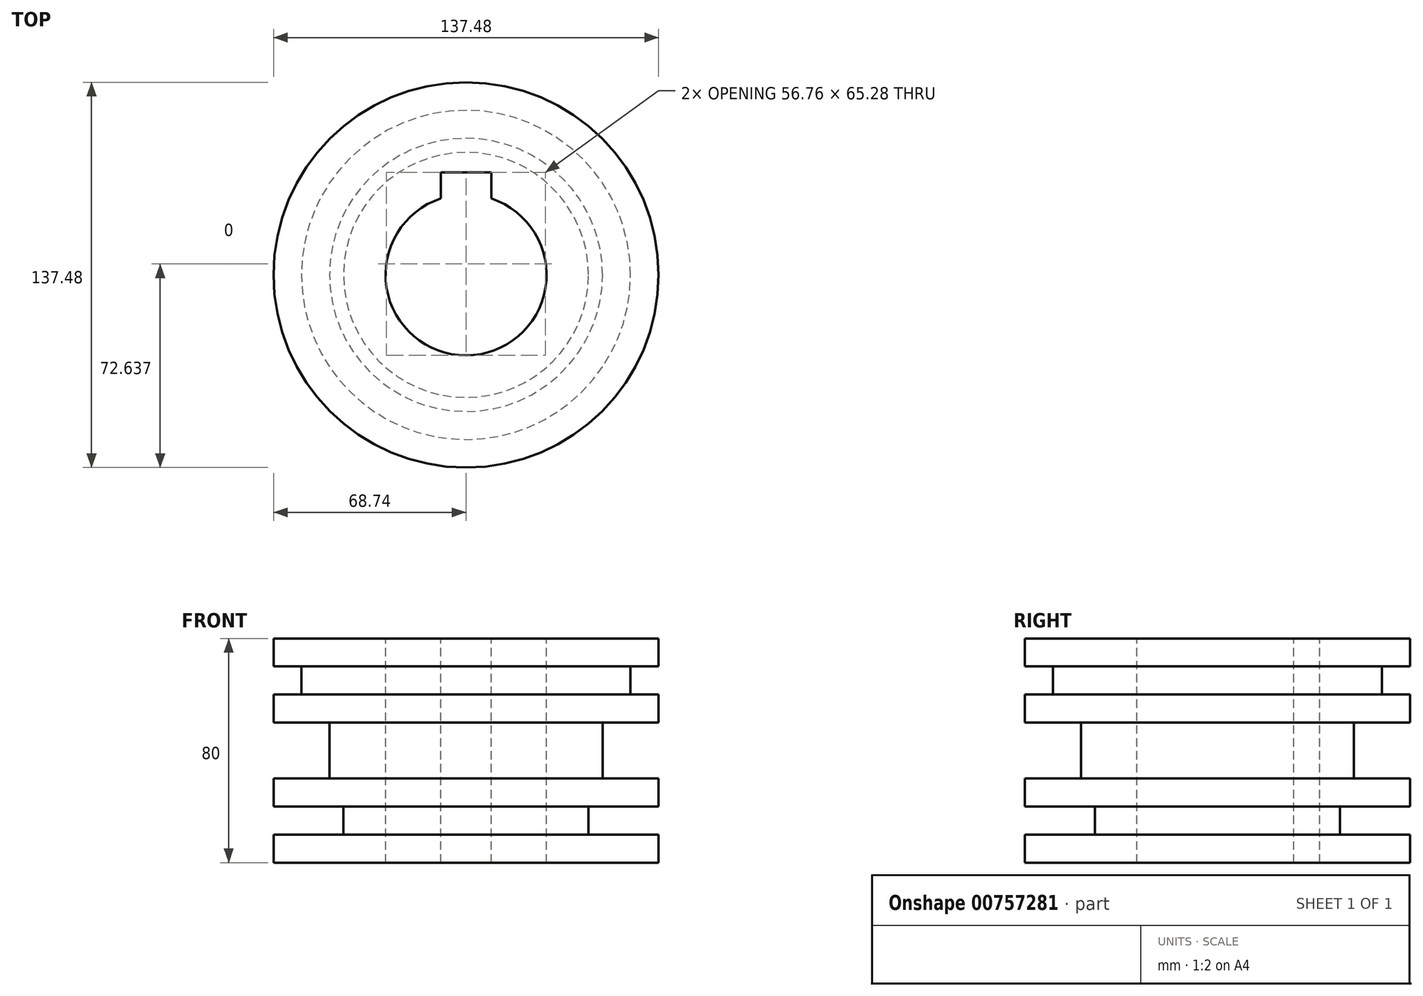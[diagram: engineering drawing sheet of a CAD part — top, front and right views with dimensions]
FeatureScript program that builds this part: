
annotation { "Feature Type Name" : "Feature", "Feature Type Description" : "" }
export const myFeature = defineFeature(function(context is Context, id is Id, definition is map)
    precondition{}
    {
        {
            var Q0;
            Q0=qCreatedBy(makeId("Front.planeOp"),FACE);
            var sketch = newSketch(context, id + "F0", { "sketchPlane" : qUnion([Q0])});
            skLineSegment(sketch, "E0", {"start": v(28.74, 0) * mm, "end": v(28.74, -80) * mm});
            skLineSegment(sketch, "E1", {"start": v(28.74, 0) * mm, "end": v(68.74, 0) * mm});
            skLineSegment(sketch, "E2", {"start": v(68.74, 0) * mm, "end": v(68.74, -10) * mm});
            skLineSegment(sketch, "E3", {"start": v(68.74, -10) * mm, "end": v(58.74, -10) * mm});
            skLineSegment(sketch, "E4", {"start": v(58.74, -10) * mm, "end": v(58.74, -20) * mm});
            skLineSegment(sketch, "E5", {"start": v(58.74, -20) * mm, "end": v(68.74, -20) * mm});
            skLineSegment(sketch, "E6", {"start": v(68.74, -20) * mm, "end": v(68.74, -30) * mm});
            skLineSegment(sketch, "E7", {"start": v(68.74, -30) * mm, "end": v(48.74, -30) * mm});
            skLineSegment(sketch, "E8", {"start": v(48.74, -30) * mm, "end": v(48.74, -50) * mm});
            skLineSegment(sketch, "E9", {"start": v(48.74, -50) * mm, "end": v(68.74, -50) * mm});
            skLineSegment(sketch, "E10", {"start": v(68.74, -50) * mm, "end": v(68.74, -60) * mm});
            skLineSegment(sketch, "E11", {"start": v(68.74, -60) * mm, "end": v(43.74, -60) * mm});
            skLineSegment(sketch, "E12", {"start": v(43.74, -60) * mm, "end": v(43.74, -70) * mm});
            skLineSegment(sketch, "E13", {"start": v(43.74, -70) * mm, "end": v(68.74, -70) * mm});
            skLineSegment(sketch, "E14", {"start": v(68.74, -70) * mm, "end": v(68.74, -80) * mm});
            skLineSegment(sketch, "E15", {"start": v(68.74, -80) * mm, "end": v(28.74, -80) * mm});
            skSolve(sketch);
        }
        {
            var Q0;
            Q0=qCreatedBy(makeId("Top.planeOp"),FACE);
            var sketch = newSketch(context, id + "F1", { "sketchPlane" : qUnion([Q0])});
            skCircle(sketch, "E16", {"center": v(0, 0) * mm, "radius": 28.5 * mm});
            skSolve(sketch);
        }
        {
            var Q0;
            Q0=makeQuery(id+"F0.imprint","IMPRINT",FACE,{"disambiguationData":[TD([[makeQuery(id+"F0.imprint","IMPRINT",EDGE,{"derivedFrom":sQuery(id+"F0.wireOp",EDGE,"E0")}),1.0]])]});
            var Q1;
            Q1=sQuery(id+"F1.wireOp",EDGE,"E16");
            sweep(context, id + "F2", {"profiles" : qUnion([Q0]), "path" : qUnion([Q1])});
        }
        {
            var Q0;
            Q0=qCreatedBy(makeId("Top.planeOp"),FACE);
            var sketch = newSketch(context, id + "F3", { "sketchPlane" : qUnion([Q0])});
            skLineSegment(sketch, "E17.bottom", {"start": v(9, 21.54) * mm, "end": v(-9, 21.54) * mm});
            skLineSegment(sketch, "E17.top", {"start": v(9, 36.54) * mm, "end": v(-9, 36.54) * mm});
            skLineSegment(sketch, "E17.left", {"start": v(9, 21.54) * mm, "end": v(9, 36.54) * mm});
            skLineSegment(sketch, "E17.right", {"start": v(-9, 21.54) * mm, "end": v(-9, 36.54) * mm});
            skPoint(sketch, "E17.middle", {"position": v(0, 29.04) * mm});
            skSolve(sketch);
        }
        {
            var Q0;
            Q0=makeQuery(id+"F3.imprint","IMPRINT",FACE,{"disambiguationData":[TD([[makeQuery(id+"F3.imprint","IMPRINT",EDGE,{"derivedFrom":sQuery(id+"F3.wireOp",EDGE,"E17.bottom")}),-1.0]])]});
            extrude(context, id + "F4", {"entities" : qUnion([Q0]), "operationType" : NewBodyOperationType.REMOVE, "endBound" : BoundingType.THROUGH_ALL, "oppositeDirection" : true, "depth" : 25 * mm, "offsetDistance" : 25 * mm});
        }
    });
